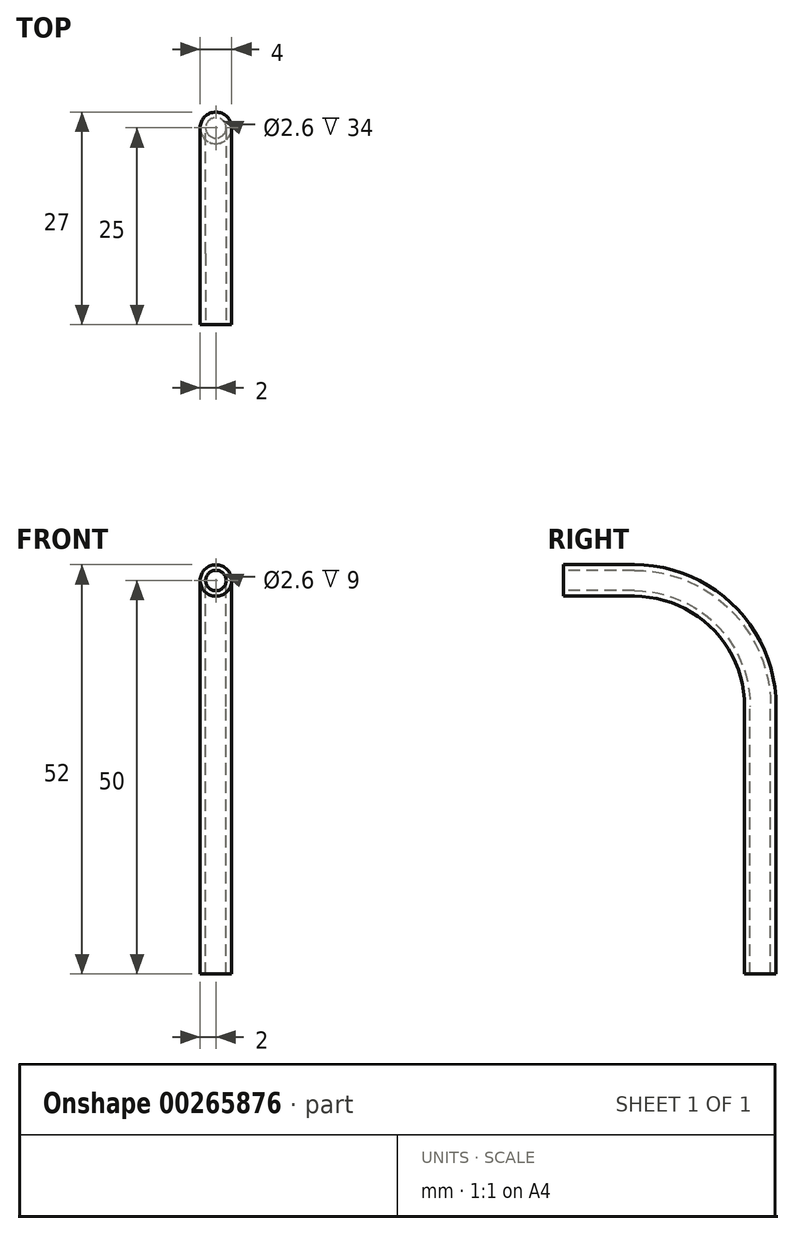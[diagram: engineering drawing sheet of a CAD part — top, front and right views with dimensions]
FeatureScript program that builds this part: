
annotation { "Feature Type Name" : "Feature", "Feature Type Description" : "" }
export const myFeature = defineFeature(function(context is Context, id is Id, definition is map)
    precondition{}
    {
        {
            var Q0;
            Q0=qCreatedBy(makeId("Top.planeOp"),FACE);
            var sketch = newSketch(context, id + "F0", { "sketchPlane" : qUnion([Q0])});
            skCircle(sketch, "E0", {"center": v(0, 0) * mm, "radius": 2 * mm});
            skCircle(sketch, "E1", {"center": v(0, 0) * mm, "radius": 1.3 * mm});
            skSolve(sketch);
        }
        {
            var Q0;
            Q0=qCreatedBy(makeId("Right.planeOp"),FACE);
            var sketch = newSketch(context, id + "F1", { "sketchPlane" : qUnion([Q0])});
            skLineSegment(sketch, "E2", {"start": v(0, 0) * mm, "end": v(0, 34) * mm});
            skLineSegment(sketch, "E3", {"start": v(-16, 50) * mm, "end": v(-25, 50) * mm});
            skPoint(sketch, "E4.visualSharp", {"position": v(0, 50) * mm});
            skArc(sketch, "E4.filletArc", {"start": v(0, 34) * mm, "mid": v(-4.69, 45.31) * mm, "end": v(-16, 50) * mm});
            skSolve(sketch);
        }
        {
            var Q0;
            Q0 = qSketchRegion(id + "F0", true);
            var Q1;
            Q1 = qConstructionFilter(qBodyType(qCreatedBy(id + "F1" ,EDGE), BodyType.WIRE), ConstructionObject.NO);
            sweep(context, id + "F2", {"profiles" : qUnion([Q0]), "path" : qUnion([Q1])});
        }
    });
